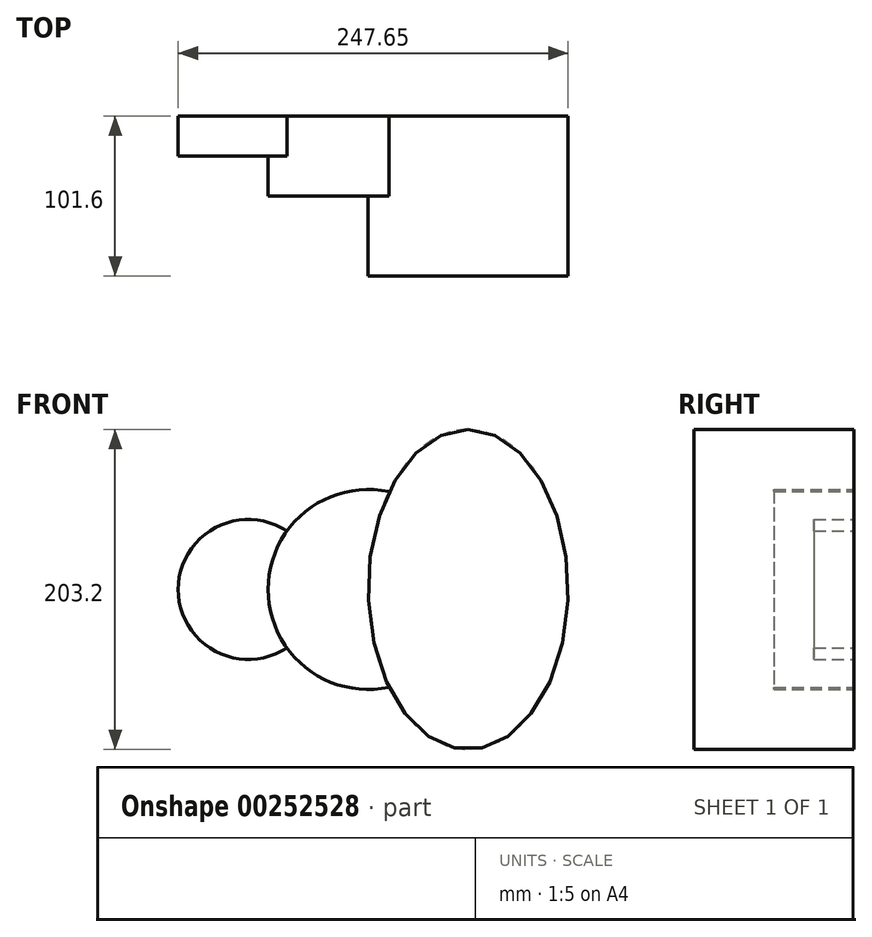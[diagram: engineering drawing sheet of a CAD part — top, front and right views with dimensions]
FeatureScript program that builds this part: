
annotation { "Feature Type Name" : "Feature", "Feature Type Description" : "" }
export const myFeature = defineFeature(function(context is Context, id is Id, definition is map)
    precondition{}
    {
        {
            var Q0;
            Q0=qCreatedBy(makeId("Front.planeOp"),FACE);
            var sketch = newSketch(context, id + "F0", { "sketchPlane" : qUnion([Q0])});
            skCircle(sketch, "E0", {"center": v(-76.2, 0) * mm, "radius": 44.45 * mm});
            skCircle(sketch, "E1", {"center": v(0, 0) * mm, "radius": 63.5 * mm});
            skLineSegment(sketch, "E2", {"start": v(63.5, 0) * mm, "end": v(63.5, 101.6) * mm});
            skEllipse(sketch, "E3", {"center": v(63.5, 0) * mm, "majorRadius": 101.6 * mm, "minorRadius": 63.5 * mm, "majorAxis": v(0, 1)});
            skSolve(sketch);
        }
        {
            var Q0;
            {var subQ0=sQuery(id+"F0.wireOp",EDGE,"E1");var subQ1=sQuery(id+"F0.wireOp",EDGE,"E0");var subQ2=makeQuery(id+"F0.imprint","INTERSECT",VERTEX,{"disambiguationData":[OD(0.0)],"derivedFrom":[subQ1,subQ0]});Q0=makeQuery(id+"F0.imprint","IMPRINT",FACE,{"disambiguationData":[TD([[makeQuery(id+"F0.imprint","IMPRINT",EDGE,{"disambiguationData":[TD([[subQ2,-1.0]])],"derivedFrom":subQ1}),1.0]])]});}
            extrude(context, id + "F1", {"entities" : qUnion([Q0]), "depth" : 25.4 * mm});
        }
        {
            var Q0;
            {var subQ0=sQuery(id+"F0.wireOp",EDGE,"E1");var subQ1=sQuery(id+"F0.wireOp",EDGE,"E0");var subQ2=makeQuery(id+"F0.imprint","INTERSECT",VERTEX,{"disambiguationData":[OD(0.0)],"derivedFrom":[subQ1,subQ0]});Q0=makeQuery(id+"F0.imprint","IMPRINT",FACE,{"disambiguationData":[TD([[makeQuery(id+"F0.imprint","IMPRINT",EDGE,{"disambiguationData":[TD([[subQ2,1.0]])],"derivedFrom":subQ1}),-1.0]])]});}
            var Q1;
            {var subQ0=sQuery(id+"F0.wireOp",EDGE,"E1");var subQ1=sQuery(id+"F0.wireOp",EDGE,"E0");var subQ2=makeQuery(id+"F0.imprint","INTERSECT",VERTEX,{"disambiguationData":[OD(0.0)],"derivedFrom":[subQ1,subQ0]});Q1=makeQuery(id+"F0.imprint","IMPRINT",FACE,{"disambiguationData":[TD([[makeQuery(id+"F0.imprint","IMPRINT",EDGE,{"disambiguationData":[TD([[subQ2,1.0]])],"derivedFrom":subQ1}),1.0]])]});}
            extrude(context, id + "F2", {"entities" : qUnion([Q0, Q1]), "operationType" : NewBodyOperationType.ADD, "depth" : 50.8 * mm});
        }
        {
            var Q0;
            {var subQ0=sQuery(id+"F0.wireOp",EDGE,"E2");Q0=makeQuery(id+"F0.imprint","IMPRINT",FACE,{"disambiguationData":[TD([[makeQuery(id+"F0.imprint","IMPRINT",EDGE,{"derivedFrom":subQ0}),1.0]])]});}
            var Q1;
            {var subQ0=sQuery(id+"F0.wireOp",EDGE,"E2");Q1=makeQuery(id+"F0.imprint","IMPRINT",FACE,{"disambiguationData":[TD([[makeQuery(id+"F0.imprint","IMPRINT",EDGE,{"derivedFrom":subQ0}),-1.0]])]});}
            var Q2;
            {var subQ0=sQuery(id+"F0.wireOp",EDGE,"E1");var subQ1=makeQuery(id+"F0.imprint","INTERSECT",VERTEX,{"derivedFrom":[subQ0,sQuery(id+"F0.wireOp",EDGE,"E2")]});Q2=makeQuery(id+"F0.imprint","IMPRINT",FACE,{"disambiguationData":[TD([[makeQuery(id+"F0.imprint","IMPRINT",EDGE,{"disambiguationData":[TD([[subQ1,-1.0]])],"derivedFrom":subQ0}),1.0]])]});}
            extrude(context, id + "F3", {"entities" : qUnion([Q0, Q1, Q2]), "operationType" : NewBodyOperationType.ADD, "depth" : 101.6 * mm});
        }
    });
